# Revit family: Sanitary_Urinals_Sanindusa_Modo-Urinal-Back-Water-Supply-And-Electronic-Spreader
name_source: partatom
category: Plumbing Fixtures
revit_build: Autodesk Revit 2018 (Build: 20170223_1515(x64)
units: mm (PartAtom-declared; Revit-internal decimal feet)

## family parameters
Always vertical = Yes
Cut with Voids When Loaded = No
Host = Wall
OmniClass Number = 23.45.00.00
OmniClass Title = Sanitary, Laundry, and Cleaning Equipment
Part Type = Normal
Room Calculation Point = No
Round Connector Dimension = Use Diameter
Shared = No

## types (1)
- SaninusaUrinal108537
    AssetType = Fixed
    Category = Pr_40_20_93_78: Urinal Cisterns
    Color = White
    Constituents = MSKT1645-KIT for Modo urinal with electronic spreader includes: 5A08537011–Modo urinal diffuser battery; 1150000–Siphon for urinal; Fixing kit; Installation kit with 850 hose with ½” F/F curve, concealed valve, 1/2" F/F, wall elbow outlet 1/2" M/M, 2 fixings for flexible and electrical wires, 2 plastic cable ties; and assembly instructions.(all included)
    Cost = 0 $
    Description = Urinal with electronic spreader
    DrainSize = 50 mm  [stored 0.164042 ft]
    Edition number = 1
    Features = Ideal for public and private spaces. Very eficient and clean with the electronic spreader. The flow is automatically activated when, after the minimum detection time has elapsed, the user moves away from the range sensor for a period longer than the set delay time. Turns off after a few seconds (flow time).
    Finish = gloss
    InletDiameter = 19 mm  [stored 0.062336 ft]
    Installation Instructions = https://www.tec.sanindusa.pt
    InstallationDate = 1900-12-31T23:59:59
    Manufacturer = Sanindusa
    ManufacturerName = Sanindusa
    ManufacturerURL = www.tec.sanindusa.pt
    Material = Vitreous China
    ModelNumber = 108537004
    ModelReference = Modo
    Name = Urinal modo with back water supply and electronic spreader
    NominalHeight = 735 mm
    NominalLength = 458 mm
    NominalWidth = 270 mm  [stored 0.885827 ft]
    Product Guid = 486a33d6-b978-4f39-8ad5-640b3a23fcb3
    Product data url = https://bimobject.com
    ProductInformation = https://www.tec.sanindusa.pt
    ProductionYear = 2017
    Size = 458x270x735
    SustainabilityPerformance = n/a
n/a
    URL = www.tec.sanindusa.pt
    Uniclass2015Code = Pr_40_20_93_78
    Uniclass2015Title = Urinal Cisterns
    Uniclass2015Version = Products v1.6
    UrinalType = Bowl
    Version = 2
    WarrantyDescription = https://www.tec.sanindusa.pt
    WarrantyDurationParts = 5
    WarrantyDurationUnit = year
    WarrantyStartDate = 1900-12-31T23:59:59
    Weight = 29.00 kg

note: [stored X ft] marks values corroborated as IEEE doubles in the binary element streams (Revit-internal decimal feet)

## geometry (parser evidence)
native form markers: Sweep x7
no freeform markers — native parametric forms only
